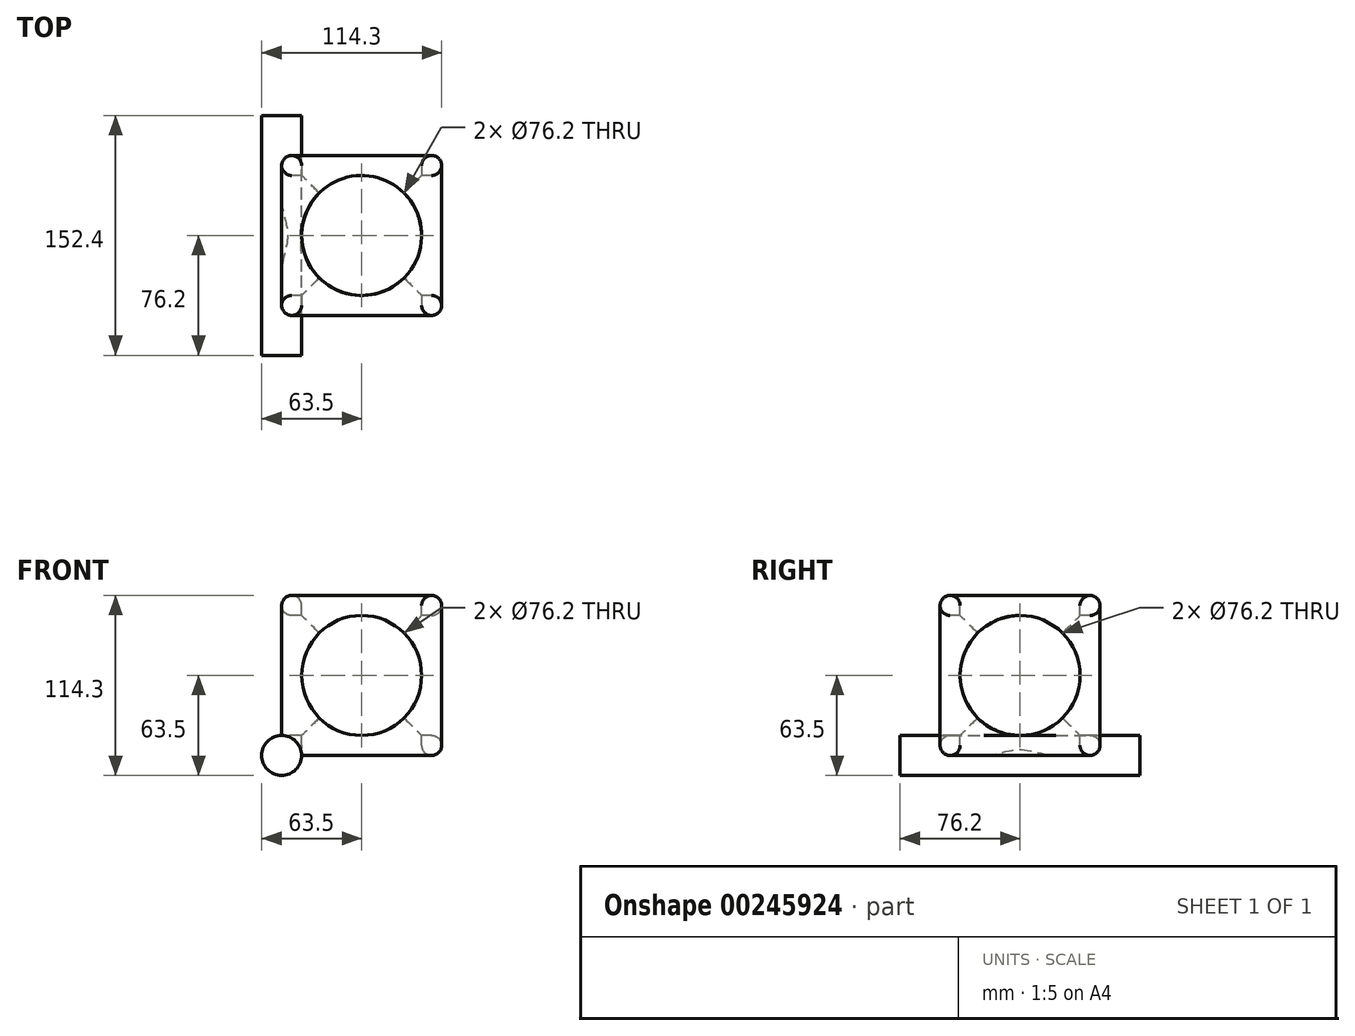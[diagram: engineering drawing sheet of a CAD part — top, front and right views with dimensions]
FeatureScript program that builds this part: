
annotation { "Feature Type Name" : "Feature", "Feature Type Description" : "" }
export const myFeature = defineFeature(function(context is Context, id is Id, definition is map)
    precondition{}
    {
        {
            var Q0;
            Q0=qCreatedBy(makeId("Front.planeOp"),FACE);
            var sketch = newSketch(context, id + "F0", { "sketchPlane" : qUnion([Q0])});
            skLineSegment(sketch, "E0", {"start": v(0, 0) * mm, "end": v(101.6, 0) * mm});
            skLineSegment(sketch, "E1", {"start": v(101.6, 0) * mm, "end": v(101.6, 101.6) * mm});
            skLineSegment(sketch, "E2", {"start": v(101.6, 101.6) * mm, "end": v(0, 101.6) * mm});
            skLineSegment(sketch, "E3", {"start": v(0, 101.6) * mm, "end": v(0, 0) * mm});
            skSolve(sketch);
        }
        {
            var Q0;
            Q0=makeQuery(id+"F0.imprint","IMPRINT",FACE,{"disambiguationData":[TD([[makeQuery(id+"F0.imprint","IMPRINT",EDGE,{"derivedFrom":sQuery(id+"F0.wireOp",EDGE,"E0")}),1.0]])]});
            extrude(context, id + "F1", {"entities" : qUnion([Q0]), "depth" : 101.6 * mm});
        }
        {
            var Q0;
            Q0=makeQuery(id+"F1.opExtrude","SWEPT_FACE",FACE,{"disambiguationData":[OSD([sQuery(id+"F0.wireOp",EDGE,"E2")])]});
            var sketch = newSketch(context, id + "F2", { "sketchPlane" : qUnion([Q0])});
            skCircle(sketch, "E4", {"center": v(50.8, -50.8) * mm, "radius": 38.1 * mm});
            skSolve(sketch);
        }
        {
            var Q0;
            Q0=makeQuery(id+"F2.imprint","IMPRINT",FACE,{"disambiguationData":[TD([[makeQuery(id+"F2.imprint","IMPRINT",EDGE,{"derivedFrom":sQuery(id+"F2.wireOp",EDGE,"E4")}),1.0]])]});
            extrude(context, id + "F3", {"entities" : qUnion([Q0]), "operationType" : NewBodyOperationType.REMOVE, "oppositeDirection" : true, "depth" : 101.6 * mm});
        }
        {
            var Q0;
            Q0=makeQuery(id+"F1.opExtrude","SWEPT_FACE",FACE,{"disambiguationData":[OSD([sQuery(id+"F0.wireOp",EDGE,"E3")])]});
            var sketch = newSketch(context, id + "F4", { "sketchPlane" : qUnion([Q0])});
            skCircle(sketch, "E5", {"center": v(50.8, 50.8) * mm, "radius": 38.1 * mm});
            skSolve(sketch);
        }
        {
            var Q0;
            Q0=makeQuery(id+"F4.imprint","IMPRINT",FACE,{"disambiguationData":[TD([[makeQuery(id+"F4.imprint","IMPRINT",EDGE,{"derivedFrom":sQuery(id+"F4.wireOp",EDGE,"E5")}),1.0]])]});
            extrude(context, id + "F5", {"entities" : qUnion([Q0]), "operationType" : NewBodyOperationType.REMOVE, "oppositeDirection" : true, "depth" : 101.6 * mm});
        }
        {
            var Q0;
            Q0=makeQuery(id+"F1.opExtrude","CAP_FACE",FACE,{"disambiguationData":[OSD([sQuery(id+"F0.wireOp",EDGE,"E0"),sQuery(id+"F0.wireOp",EDGE,"E1"),sQuery(id+"F0.wireOp",EDGE,"E2"),sQuery(id+"F0.wireOp",EDGE,"E3")])],"isStart":false});
            var sketch = newSketch(context, id + "F6", { "sketchPlane" : qUnion([Q0])});
            skCircle(sketch, "E6", {"center": v(50.8, 50.8) * mm, "radius": 38.1 * mm});
            skSolve(sketch);
        }
        {
            var Q0;
            Q0=makeQuery(id+"F6.imprint","IMPRINT",FACE,{"disambiguationData":[TD([[makeQuery(id+"F6.imprint","IMPRINT",EDGE,{"derivedFrom":sQuery(id+"F6.wireOp",EDGE,"E6")}),1.0]])]});
            extrude(context, id + "F7", {"entities" : qUnion([Q0]), "operationType" : NewBodyOperationType.REMOVE, "oppositeDirection" : true, "depth" : 101.6 * mm});
        }
        {
            var Q0;
            Q0=makeQuery(id+"F1.opExtrude","SWEPT_FACE",FACE,{"disambiguationData":[OSD([sQuery(id+"F0.wireOp",EDGE,"E2")])]});
            var Q1;
            Q1=makeQuery(id+"F1.opExtrude","CAP_FACE",FACE,{"disambiguationData":[OSD([sQuery(id+"F0.wireOp",EDGE,"E0"),sQuery(id+"F0.wireOp",EDGE,"E1"),sQuery(id+"F0.wireOp",EDGE,"E2"),sQuery(id+"F0.wireOp",EDGE,"E3")])],"isStart":false});
            var Q2;
            Q2=makeQuery(id+"F1.opExtrude","SWEPT_FACE",FACE,{"disambiguationData":[OSD([sQuery(id+"F0.wireOp",EDGE,"E1")])]});
            var Q3;
            Q3=makeQuery(id+"F1.opExtrude","CAP_FACE",FACE,{"disambiguationData":[OSD([sQuery(id+"F0.wireOp",EDGE,"E0"),sQuery(id+"F0.wireOp",EDGE,"E1"),sQuery(id+"F0.wireOp",EDGE,"E2"),sQuery(id+"F0.wireOp",EDGE,"E3")])],"isStart":true});
            var Q4;
            Q4=makeQuery(id+"F1.opExtrude","SWEPT_FACE",FACE,{"disambiguationData":[OSD([sQuery(id+"F0.wireOp",EDGE,"E3")])]});
            var Q5;
            Q5=makeQuery(id+"F1.opExtrude","SWEPT_FACE",FACE,{"disambiguationData":[OSD([sQuery(id+"F0.wireOp",EDGE,"E0")])]});
            fillet(context, id + "F8", {"entities" : qUnion([Q0, Q1, Q2, Q3, Q4, Q5]), "radius" : 6.35 * mm, "tangentPropagation" : true, "allowEdgeOverflow" : false});
        }
        {
            var Q0;
            Q0=qCreatedBy(makeId("Front.planeOp"),FACE);
            cPlane(context, id + "F9", {"entities" : qUnion([Q0]), "cplaneType" : CPlaneType.OFFSET, "offset" : 101.6 * mm, "width" : 152.4 * mm, "height" : 152.4 * mm});
        }
        {
            var Q0;
            Q0=qCreatedBy(id+"F9.planeOp",FACE);
            var sketch = newSketch(context, id + "F10", { "sketchPlane" : qUnion([Q0])});
            skCircle(sketch, "E7", {"center": v(0, 0) * mm, "radius": 12.7 * mm});
            skSolve(sketch);
        }
        {
            var Q0;
            Q0=makeQuery(id+"F10.imprint","IMPRINT",FACE,{"disambiguationData":[TD([[makeQuery(id+"F10.imprint","IMPRINT",EDGE,{"derivedFrom":sQuery(id+"F10.wireOp",EDGE,"E7")}),1.0]])]});
            extrude(context, id + "F11", {"entities" : qUnion([Q0]), "operationType" : NewBodyOperationType.ADD, "depth" : 25.4 * mm, "hasSecondDirection" : true, "secondDirectionOppositeDirection" : true, "secondDirectionDepth" : 127 * mm});
        }
    });
